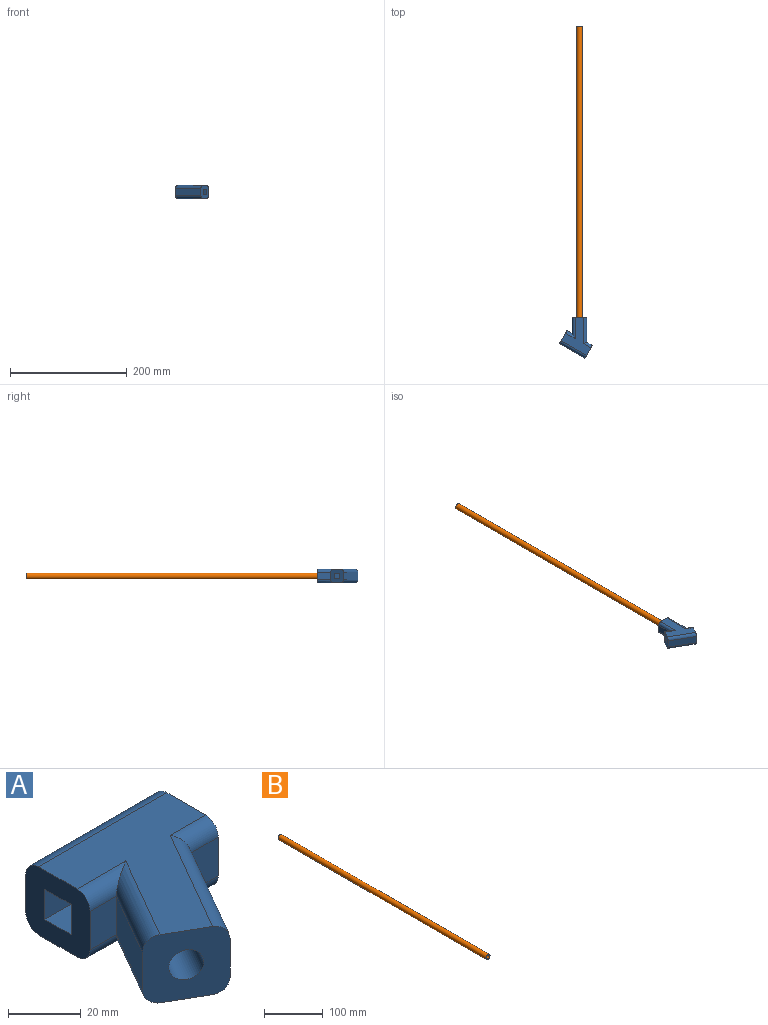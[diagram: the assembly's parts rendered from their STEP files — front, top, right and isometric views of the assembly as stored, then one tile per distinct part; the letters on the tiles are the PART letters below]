
ASSEMBLY  parts=2 mates=1
PART A: 25 faces, bbox 54.8x62.8x24.2 mm
  f0: plane 13x10.84mm, normal (0,-1,0), area 141mm2, adj f3,f11,f15,f17
  f1: plane 25x23mm, normal (-1,0,0), area 449.5mm2, adj f2,f4,f5,f6,f7,f8,f9,f10
  f2: plane 13x10.29mm, normal (0,-1,0), area 133.8mm2, adj f1,f12,f18,f20
  f3: plane 25x23mm, normal (1,0,0), area 449.5mm2, adj f0,f4,f5,f6,f7,f8,f9,f10
  f4: plane 50x13mm, normal (0,1,0), area 650mm2, adj f1,f3,f22,f23
  f5: plane 54.06x50mm, normal (0,0,1), area 1361.6mm2, adj f1,f3,f13,f14,f15,f18,f19,f23
  f6: plane 54.06x50mm, normal (0,0,-1), area 1361.6mm2, adj f1,f3,f13,f16,f17,f20,f21,f22
  f7: plane 50x10.2mm, normal (0,-1,0), area 510mm2, adj f1,f3,f8,f10
  f8: plane 50x10.2mm, normal (0,0,-1), area 510mm2, adj f1,f3,f7,f9
  f9: plane 51.21x11.41mm, normal (0,1,0), area 419.3mm2, adj f1,f3,f8,f10,f24
  f10: plane 50x10.2mm, normal (0,0,1), area 510mm2, adj f1,f3,f7,f9
  f11: plane 36.56x21.11mm, normal (0.87,-0.5,0), area 548.8mm2, adj f0,f13,f14,f16
  f12: plane 24.06x13.89mm, normal (-0.87,0.5,0), area 361.2mm2, adj f2,f13,f19,f21
  f13: plane 23x21.65mm, normal (-0.5,-0.87,0), area 475mm2, adj f5,f6,f11,f12,f14,f16,f19,f21
  f14: cylinder r=5mm len=41.56mm, axis (0.5,0.87,0), area 342.9mm2, adj f5,f11,f13,f15
  f15: cylinder r=5mm len=13.73mm, axis (-1,0,0), area 96.5mm2, adj f0,f3,f5,f14
  f16: cylinder r=5mm len=41.56mm, axis (-0.5,-0.87,0), area 342.9mm2, adj f6,f11,f13,f17
  f17: cylinder r=5mm len=13.73mm, axis (1,0,0), area 96.5mm2, adj f0,f3,f6,f16
  f18: cylinder r=5mm len=18.95mm, axis (-1,0,0), area 105.5mm2, adj f1,f2,f5,f19
  f19: cylinder r=5mm len=34.06mm, axis (-0.5,-0.87,0), area 242.9mm2, adj f5,f12,f13,f18
  f20: cylinder r=5mm len=18.95mm, axis (1,0,0), area 105.5mm2, adj f1,f2,f6,f21
  f21: cylinder r=5mm len=34.06mm, axis (0.5,0.87,0), area 242.9mm2, adj f6,f12,f13,f20
  f22: cylinder r=5mm len=50mm, axis (-1,0,0), area 392.7mm2, adj f1,f3,f4,f6
  f23: cylinder r=5mm len=50mm, axis (1,0,0), area 392.7mm2, adj f1,f3,f4,f5
  f24: cylinder r=5mm len=45.21mm, axis (-0.5,-0.87,0), area 1368mm2, adj f9,f13
PART B: 4 faces, bbox 10x500x10 mm
  f0: cylinder r=4mm len=500mm, axis (0,1,0), area 12566.4mm2, adj f2,f3
  f1: cylinder r=5mm len=500mm, axis (0,1,0), area 15708mm2, adj f2,f3
  f2: plane 10x10mm, normal (0,-1,0), area 28.3mm2, adj f0,f1
  f3: plane 10x10mm, normal (0,1,0), area 28.3mm2, adj f0,f1
PLACE A rot(axis=(0.97,-0.26,0),180deg) t=(37.54,-482.91,2.22)mm
PLACE B rot(axis=(1,0,0),180deg) t=(16.45,-201.89,-9.28)mm
MATE fastened B.f0 <-> A.f24  axis (0,-1,0) through (16.45,-451.89,-9.28)mm
